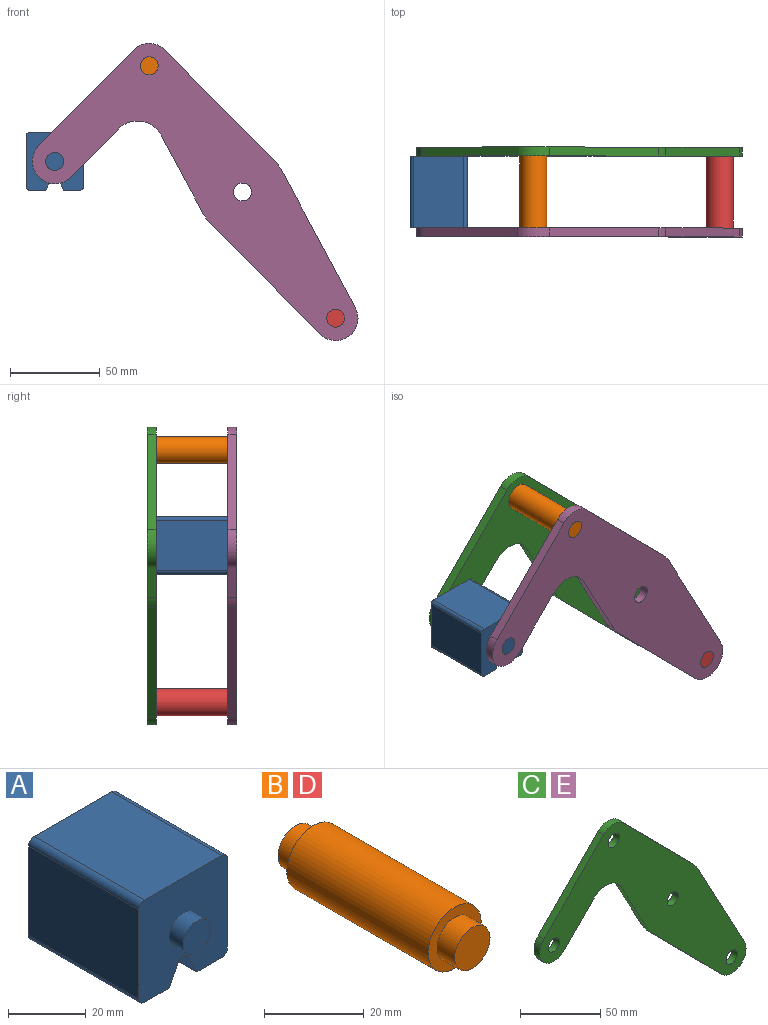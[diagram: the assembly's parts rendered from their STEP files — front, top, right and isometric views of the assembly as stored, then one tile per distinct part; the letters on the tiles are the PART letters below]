
ASSEMBLY  parts=5 mates=4
PART A: 18 faces, bbox 32.1x50x32.1 mm
  f0: plane 40x28.08mm, normal (1,0,0), area 1123.1mm2, adj f4,f10,f13,f14
  f1: plane 40x9.04mm, normal (0,0,-1), area 361.6mm2, adj f2,f4,f10,f14
  f2: plane 40x6.42mm, normal (-0.89,0,-0.45), area 287.2mm2, adj f1,f4,f10,f15
  f3: plane 40x6.42mm, normal (0.89,0,-0.45), area 287.2mm2, adj f4,f5,f10,f15
  f4: plane 32.08x32.08mm, normal (0,-1,0), area 900.6mm2, adj f0,f1,f2,f3,f5,f6,f7,f9
  f5: plane 40x9.04mm, normal (0,0,-1), area 361.6mm2, adj f3,f4,f10,f16
  f6: plane 40x28.08mm, normal (0,0,1), area 1123.1mm2, adj f4,f10,f13,f17
  f7: plane 40x28.08mm, normal (-1,0,0), area 1123.1mm2, adj f4,f10,f16,f17
  f8: plane 10x10mm, normal (0,-1,0), area 78.5mm2, adj f9
  f9: cylinder r=5mm len=10mm, axis (0,1,0), area 157.1mm2, adj f4,f8
  f10: plane 32.08x32.08mm, normal (0,1,0), area 900.6mm2, adj f0,f1,f2,f3,f5,f6,f7,f12
  f11: plane 10x10mm, normal (0,1,0), area 78.5mm2, adj f12
  f12: cylinder r=5mm len=10mm, axis (0,-1,0), area 157.1mm2, adj f10,f11
  f13: cylinder r=2mm len=40mm, axis (0,1,0), area 125.7mm2, adj f0,f4,f6,f10
  f14: cylinder r=2mm len=40mm, axis (0,-1,0), area 125.7mm2, adj f0,f1,f4,f10
  f15: cylinder r=2mm len=40mm, axis (0,1,0), area 177.1mm2, adj f2,f3,f4,f10
  f16: cylinder r=2mm len=40mm, axis (0,1,0), area 125.7mm2, adj f4,f5,f7,f10
  f17: cylinder r=2mm len=40mm, axis (0,-1,0), area 125.7mm2, adj f4,f6,f7,f10
PART B: 7 faces, bbox 15x50x15 mm
  f0: cylinder r=7.5mm len=40mm, axis (0,-1,0), area 1885mm2, adj f2,f5
  f1: cylinder r=5mm len=10mm, axis (0,1,0), area 157.1mm2, adj f2,f3
  f2: plane 15x15mm, normal (0,-1,0), area 98.2mm2, adj f0,f1
  f3: plane 10x10mm, normal (0,-1,0), area 78.5mm2, adj f1
  f4: cylinder r=5mm len=10mm, axis (0,-1,0), area 157.1mm2, adj f5,f6
  f5: plane 15x15mm, normal (0,1,0), area 98.2mm2, adj f0,f4
  f6: plane 10x10mm, normal (0,1,0), area 78.5mm2, adj f4
PART C: 18 faces, bbox 181.7x5x165.8 mm
  f0: plane 43.49x23.35mm, normal (-0.88,0,-0.47), area 246.8mm2, adj f1,f14,f16,f17
  f1: cylinder r=25mm len=5.75mm, axis (0,1,0), area 35.8mm2, adj f0,f2,f16,f17
  f2: plane 61.6x60.87mm, normal (-0.71,0,-0.7), area 433mm2, adj f1,f3,f16,f17
  f3: cylinder r=12.5mm len=21.39mm, axis (0,1,0), area 178.4mm2, adj f2,f4,f16,f17
  f4: plane 76.3x40.96mm, normal (0.88,0,0.47), area 433mm2, adj f3,f5,f16,f17
  f5: cylinder r=25mm len=5.75mm, axis (0,1,0), area 35.8mm2, adj f4,f6,f16,f17
  f6: plane 61.6x60.87mm, normal (0.71,0,0.7), area 433mm2, adj f5,f7,f16,f17
  f7: cylinder r=12.5mm len=17.78mm, axis (0,1,0), area 98.9mm2, adj f6,f8,f16,f17
  f8: plane 53.35x52.71mm, normal (-0.71,0,0.7), area 375mm2, adj f7,f9,f16,f17
  f9: cylinder r=12.5mm len=21.39mm, axis (0,1,0), area 196.3mm2, adj f8,f10,f16,f17
  f10: plane 26.86x26.54mm, normal (0.71,0,-0.7), area 188.8mm2, adj f9,f14,f16,f17
  f11: cylinder r=5mm len=10mm, axis (0,1,0), area 157.1mm2, adj f16,f17
  f12: cylinder r=5mm len=10mm, axis (0,1,0), area 157.1mm2, adj f16,f17
  f13: cylinder r=5mm len=10mm, axis (0,1,0), area 157.1mm2, adj f16,f17
  f14: cylinder r=15mm len=23.89mm, axis (0,1,0), area 140.2mm2, adj f0,f10,f16,f17
  f15: cylinder r=5mm len=10mm, axis (0,1,0), area 157.1mm2, adj f16,f17
  f16: plane 181.66x165.78mm, normal (0,-1,0), area 8710.1mm2, adj f0,f1,f2,f3,f4,f5,f6,f7
  f17: plane 181.66x165.78mm, normal (0,1,0), area 8710.1mm2, adj f0,f1,f2,f3,f4,f5,f6,f7
PART D: same geometry as B
PART E: same geometry as C
PLACE A t=(-3.19,-24.1,-6.69)mm
PLACE B t=(-3.19,-24.1,-6.69)mm
PLACE C t=(-3.19,20.9,-6.69)mm
PLACE D t=(100.76,-24.1,-147.47)mm
PLACE E t=(-3.19,-24.1,-6.69)mm fixed
MATE fastened B.f0 <-> E.f7  axis (0,-1,0) through (-55.17,-24.1,63.7)mm
MATE revolute A.f9 <-> E.f9  axis (0,-1,0) through (-107.88,-24.1,10.35)mm
MATE fastened D.f0 <-> E.f3  axis (0,-1,0) through (48.78,-24.1,-77.08)mm
MATE fastened C.f7 <-> B.f0  axis (0,-1,0) through (-55.17,15.9,63.7)mm
